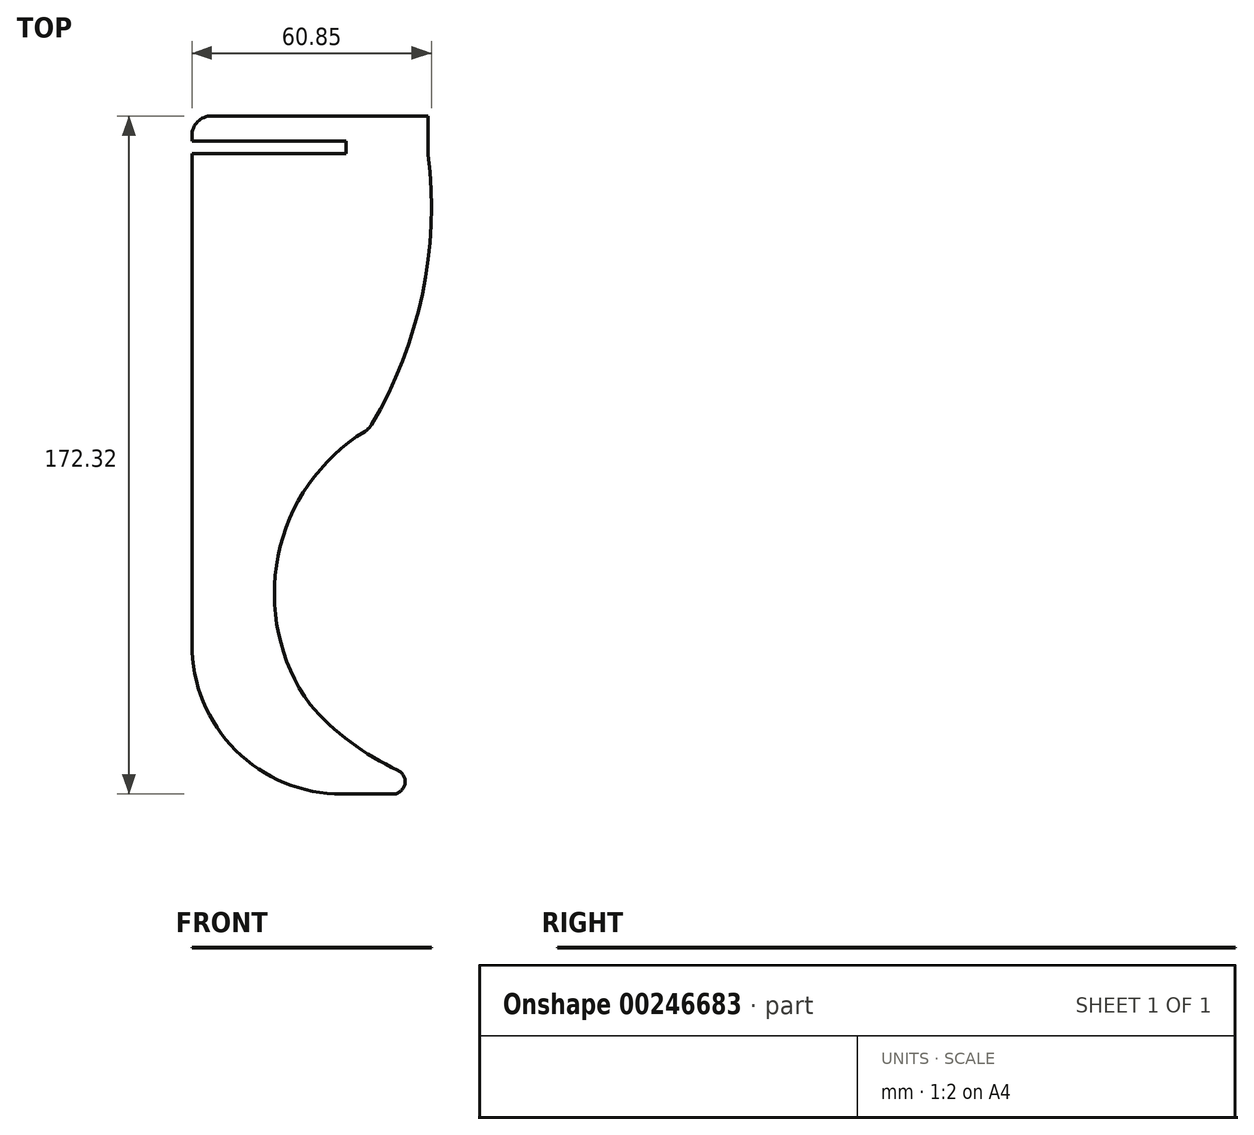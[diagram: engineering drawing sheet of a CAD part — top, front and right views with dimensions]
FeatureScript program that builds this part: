
annotation { "Feature Type Name" : "Feature", "Feature Type Description" : "" }
export const myFeature = defineFeature(function(context is Context, id is Id, definition is map)
    precondition{}
    {
        {
            var Q0;
            Q0=qCreatedBy(makeId("Top.planeOp"),FACE);
            var sketch = newSketch(context, id + "F0", { "sketchPlane" : qUnion([Q0])});
            skLineSegment(sketch, "E0.bottom", {"start": v(0, 0) * mm, "end": v(39.23, 0) * mm});
            skLineSegment(sketch, "E0.top", {"start": v(0, 6.35) * mm, "end": v(60, 6.35) * mm});
            skLineSegment(sketch, "E0.left", {"start": v(0, 0) * mm, "end": v(0, 6.35) * mm});
            skLineSegment(sketch, "E0.right", {"start": v(60, 0) * mm, "end": v(60, 6.35) * mm});
            skLineSegment(sketch, "E1.bottom", {"start": v(60, 6.35) * mm, "end": v(39.23, 6.35) * mm});
            skLineSegment(sketch, "E1.left", {"start": v(60, 6.35) * mm, "end": v(60, -3.17) * mm});
            skLineSegment(sketch, "E1.right", {"start": v(39.23, 0) * mm, "end": v(39.23, -3.17) * mm});
            skLineSegment(sketch, "E2.bottom", {"start": v(39.23, -3.17) * mm, "end": v(0, -3.18) * mm});
            skLineSegment(sketch, "E2.right", {"start": v(0, -3.18) * mm, "end": v(0, -30.53) * mm});
            skPoint(sketch, "E3.endSnap0", {"position": v(47.78, -0.17) * mm});
            skLineSegment(sketch, "E4", {"start": v(0, -30.53) * mm, "end": v(0, -127.87) * mm});
            skLineSegment(sketch, "E5", {"start": v(30, -3.17) * mm, "end": v(30, -124.11) * mm, "construction": true});
            skLineSegment(sketch, "E6", {"start": v(45, -3.17) * mm, "end": v(45, -120.89) * mm, "construction": true});
            skLineSegment(sketch, "E7", {"start": v(60, -3.18) * mm, "end": v(30, -143.18) * mm, "construction": true});
            skArc(sketch, "E8", {"start": v(45, -73.17) * mm, "mid": v(58.45, -39.45) * mm, "end": v(60, -3.18) * mm});
            skLineSegment(sketch, "E9", {"start": v(38.1, -165.97) * mm, "end": v(51.01, -165.97) * mm});
            skArc(sketch, "E10", {"start": v(30, -143.18) * mm, "mid": v(40.28, -152.73) * mm, "end": v(52.34, -159.91) * mm});
            skArc(sketch, "E11", {"start": v(45, -73.18) * mm, "mid": v(22.03, -104.86) * mm, "end": v(30, -143.18) * mm});
            skPoint(sketch, "E12.visualSharp", {"position": v(80.02, -165.96) * mm});
            skArc(sketch, "E12.filletArc", {"start": v(51.01, -165.97) * mm, "mid": v(54.11, -163.47) * mm, "end": v(52.34, -159.91) * mm});
            skPoint(sketch, "E13.visualSharp", {"position": v(0, -165.98) * mm});
            skArc(sketch, "E13.filletArc", {"start": v(0, -127.87) * mm, "mid": v(11.16, -154.82) * mm, "end": v(38.1, -165.97) * mm});
            skSolve(sketch);
        }
        {
            var Q0;
            Q0 = qSketchRegion(id + "F0", true);
            extrude(context, id + "F1", {"entities" : qUnion([Q0]), "depth" : 1 / 203.2 * mm});
        }
        {
            var Q0;
            Q0=makeQuery(id+"F1.opExtrude","SWEPT_EDGE",EDGE,{"disambiguationData":[OSD([sQuery(id+"F0.wireOp",EDGE,"E1.bottom"),sQuery(id+"F0.wireOp",EDGE,"E1.left")])]});
            var Q1;
            Q1=makeQuery(id+"F1.opExtrude","SWEPT_EDGE",EDGE,{"disambiguationData":[OSD([sQuery(id+"F0.wireOp",EDGE,"E0.top"),sQuery(id+"F0.wireOp",EDGE,"E0.left")])]});
            var Q2;
            Q2=makeQuery(id+"F1.opExtrude","SWEPT_EDGE",EDGE,{"disambiguationData":[OSD([sQuery(id+"F0.wireOp",EDGE,"E8"),sQuery(id+"F0.wireOp",EDGE,"E11")])]});
            fillet(context, id + "F2", {"entities" : qUnion([Q0, Q1, Q2]), "radius" : 5.08 * mm, "tangentPropagation" : true, "allowEdgeOverflow" : false});
        }
    });
